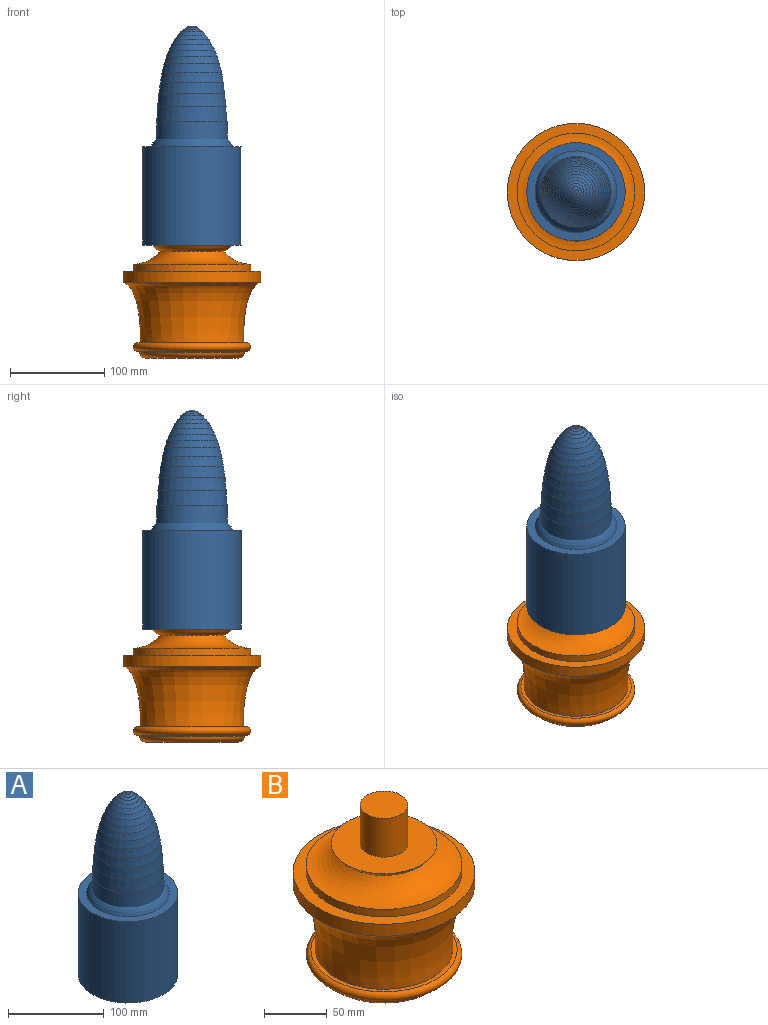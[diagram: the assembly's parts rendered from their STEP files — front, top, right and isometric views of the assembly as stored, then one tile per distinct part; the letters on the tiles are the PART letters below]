
ASSEMBLY  parts=2 mates=1
PART A: 23 faces, bbox 104.3x104.3x232.3 mm
  f0: plane 104.31x104.31mm, normal (0,0,1), area 2651.5mm2, adj f1,f22
  f1: revolved ~86.63x86.63mm, area 6861.8mm2, adj f0,f2
  f2: cone r=37.28mm half-angle=3.3deg, axis (0,0,-1), area 3725.3mm2, adj f1,f3
  f3: cone r=36.34mm half-angle=5.2deg, axis (0,0,-1), area 3126.7mm2, adj f2,f4
  f4: cone r=35.07mm half-angle=7.6deg, axis (0,0,-1), area 2628mm2, adj f3,f5
  f5: cone r=33.45mm half-angle=10.2deg, axis (0,0,-1), area 2161.1mm2, adj f4,f6
  f6: cone r=31.58mm half-angle=13.9deg, axis (0,0,-1), area 1769.4mm2, adj f5,f7
  f7: cone r=29.37mm half-angle=17.6deg, axis (0,0,-1), area 1444mm2, adj f6,f8
  f8: cone r=26.91mm half-angle=21.6deg, axis (0,0,-1), area 1183.7mm2, adj f7,f9
  f9: cone r=24.19mm half-angle=26.3deg, axis (0,0,-1), area 956.1mm2, adj f8,f10
  f10: cone r=21.21mm half-angle=29.9deg, axis (0,0,-1), area 760.2mm2, adj f9,f11
  f11: cone r=18.15mm half-angle=35.7deg, axis (0,0,-1), area 574.3mm2, adj f10,f12
  f12: cone r=14.92mm half-angle=41.6deg, axis (0,0,-1), area 406.8mm2, adj f11,f13
  f13: cone r=11.69mm half-angle=48.4deg, axis (0,0,-1), area 267.5mm2, adj f12,f14
  f14: cone r=8.54mm half-angle=56.4deg, axis (0,0,-1), area 161.9mm2, adj f13,f15
  f15: cone r=5.49mm half-angle=69.2deg, axis (0,0,-1), area 78.5mm2, adj f14,f16
  f16: cone r=2.59mm half-angle=86.2deg, axis (0,0,-1), area 21.2mm2, adj f15,f17
  f17: cone r=0.05mm half-angle=85.6deg, axis (0,0,1), area 0mm2, adj f16
  f18: plane 7.88x7.88mm, normal (0,0,-1), area 48.8mm2, adj f19
  f19: cone r=3.94mm half-angle=14.6deg, axis (0,0,-1), area 4767.8mm2, adj f18,f20
  f20: cylinder r=19.94mm len=151.47mm, axis (0,0,-1), area 18979.5mm2, adj f19,f21
  f21: plane 104.31x104.31mm, normal (0,0,-1), area 7296.1mm2, adj f20,f22
  f22: cylinder r=52.15mm len=104.43mm, axis (0,0,-1), area 34221.4mm2, adj f0,f21
PART B: 19 faces, bbox 186x186x157.9 mm
  f0: cylinder r=45.09mm len=90.17mm, axis (0,0,1), area 14370mm2, adj f4,f5,f17
  f1: revolved ~145.57x145.57mm, area 25878.1mm2, adj f10,f11,f18
  f2: cylinder r=19.05mm len=38.1mm, axis (0,0,1), area 4529.7mm2, adj f3,f16
  f3: plane 38.1x38.1mm, normal (0,0,1), area 1140.1mm2, adj f2
  f4: revolved ~90.17x45.09mm, area 0mm2, adj f0
  f5: cone r=49.34mm half-angle=89.9deg, axis (0,0,-1), area 1261.7mm2, adj f0,f6
  f6: torus R=49.35mm, axis (0,0,1), area 3187.2mm2, adj f5,f7
  f7: torus R=57.55mm, axis (0,0,1), area 765.7mm2, adj f6,f8
  f8: plane 117.06x117.06mm, normal (0,0,-1), area 508.9mm2, adj f7,f9
  f9: torus R=57.81mm, axis (0,0,1), area 4711.8mm2, adj f8,f10
  f10: plane 117.06x117.06mm, normal (0,0,1), area 1284.1mm2, adj f1,f9
  f11: cylinder r=72.78mm len=145.57mm, axis (0,0,1), area 5350.6mm2, adj f1,f12
  f12: plane 145.57x145.57mm, normal (0,0,1), area 4400.5mm2, adj f11,f13
  f13: cylinder r=62.42mm len=124.85mm, axis (0,0,1), area 2853.8mm2, adj f12,f14
  f14: torus R=61.47mm, axis (0,0,1), area 9732.7mm2, adj f13,f15
  f15: torus R=29.41mm, axis (0,0,1), area 2647.2mm2, adj f14,f16
  f16: plane 84.36x84.36mm, normal (0,0,1), area 4449.6mm2, adj f2,f15
  f17: cylinder r=2.55mm len=7.61mm, axis (1,0,0), area 121.4mm2, adj f0,f18
  f18: cone r=2.55mm half-angle=41deg, axis (1,0,0), area 68.1mm2, adj f1,f17
PLACE A t=(112.55,61.8,92.78)mm
PLACE B t=(126.66,61.8,-46.72)mm fixed
MATE slider A.f2 <-> B.f0  axis (0,0,-1) through (86.47,61.8,-23.37)mm
